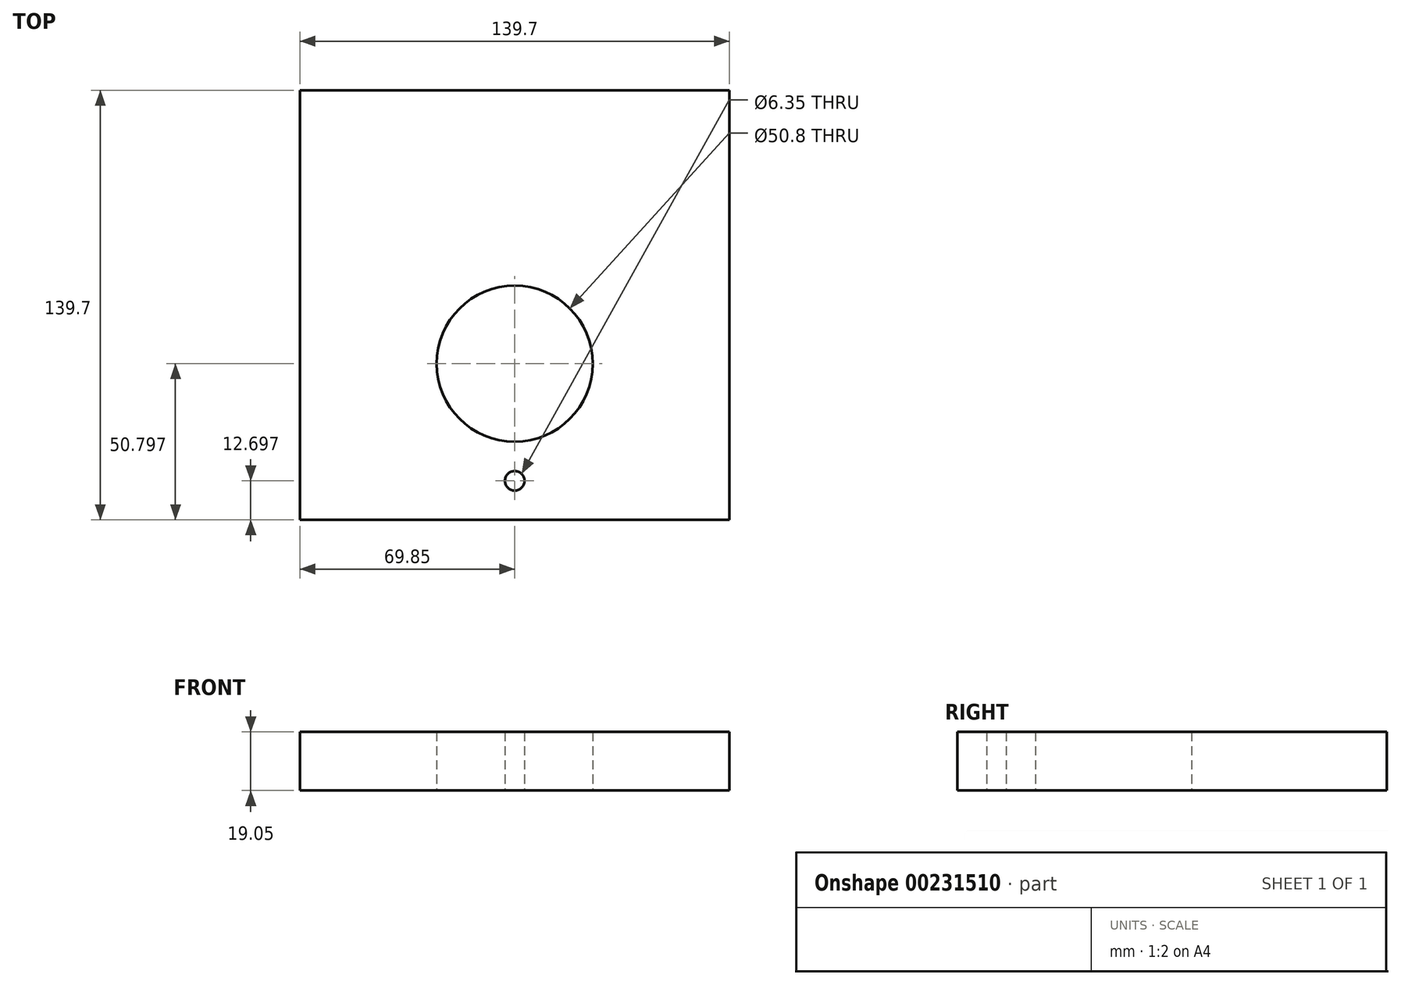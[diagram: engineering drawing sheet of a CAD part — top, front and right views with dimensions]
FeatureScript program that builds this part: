
annotation { "Feature Type Name" : "Feature", "Feature Type Description" : "" }
export const myFeature = defineFeature(function(context is Context, id is Id, definition is map)
    precondition{}
    {
        {
            var Q0;
            Q0=qCreatedBy(makeId("Top.planeOp"),FACE);
            var sketch = newSketch(context, id + "F0", { "sketchPlane" : qUnion([Q0])});
            skLineSegment(sketch, "E0.bottom", {"start": v(-69.85, -70.1) * mm, "end": v(69.85, -70.1) * mm});
            skLineSegment(sketch, "E0.top", {"start": v(-69.85, 69.6) * mm, "end": v(69.85, 69.6) * mm});
            skLineSegment(sketch, "E0.left", {"start": v(-69.85, -70.1) * mm, "end": v(-69.85, 69.6) * mm});
            skLineSegment(sketch, "E0.right", {"start": v(69.85, -70.1) * mm, "end": v(69.85, 69.6) * mm});
            skPoint(sketch, "E0.middle", {"position": v(0, -0.25) * mm});
            skLineSegment(sketch, "E1", {"start": v(0, -70.1) * mm, "end": v(0, -57.4) * mm});
            skPoint(sketch, "E1.endSnap0", {"position": v(0, -70.1) * mm});
            skLineSegment(sketch, "E2", {"start": v(0, -57.4) * mm, "end": v(0, -19.3) * mm});
            skCircle(sketch, "E3", {"center": v(0, -19.3) * mm, "radius": 25.4 * mm});
            skCircle(sketch, "E4", {"center": v(0, -57.4) * mm, "radius": 3.18 * mm});
            skSolve(sketch);
        }
        {
            var Q0;
            Q0 = qSketchRegion(id + "F0", true);
            extrude(context, id + "F1", {"entities" : qUnion([Q0]), "depth" : 19.05 * mm});
        }
    });
